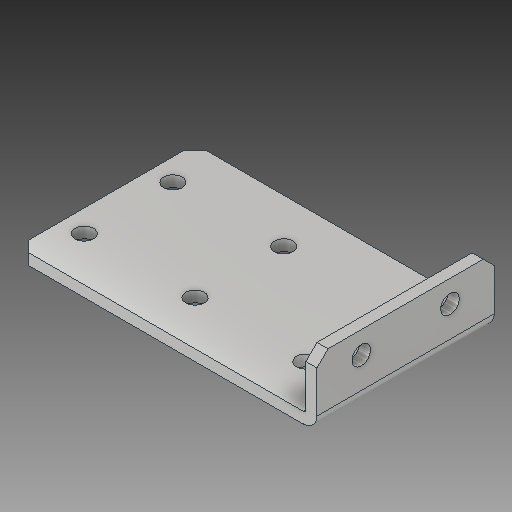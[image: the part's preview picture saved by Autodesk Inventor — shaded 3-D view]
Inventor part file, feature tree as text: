
AUTODESK INVENTOR PART (.ipt)
format: ipt  version: 2018 (Build 220112000, 112)  size: 129,024 bytes
history: native  units: in
note: dims shown in document units (in); Inventor stores cm internally (conversion verified against a paired STEP export)
features: chamfer x1
ambient origin geometry x8: Origin, YZ Plane, XZ Plane, XY Plane, X Axis, Y Axis, Z Axis, Center Point
bodies: Solid1 (feature_tree)
feature tree (1):
  chamfer  "Chamfer2"  [1 undecoded]
note: 1 required parameter value undecoded (feature->parameter linkage not recoverable at this tier; creation-order binding heuristic only, values carry confidence <= 0.55)
